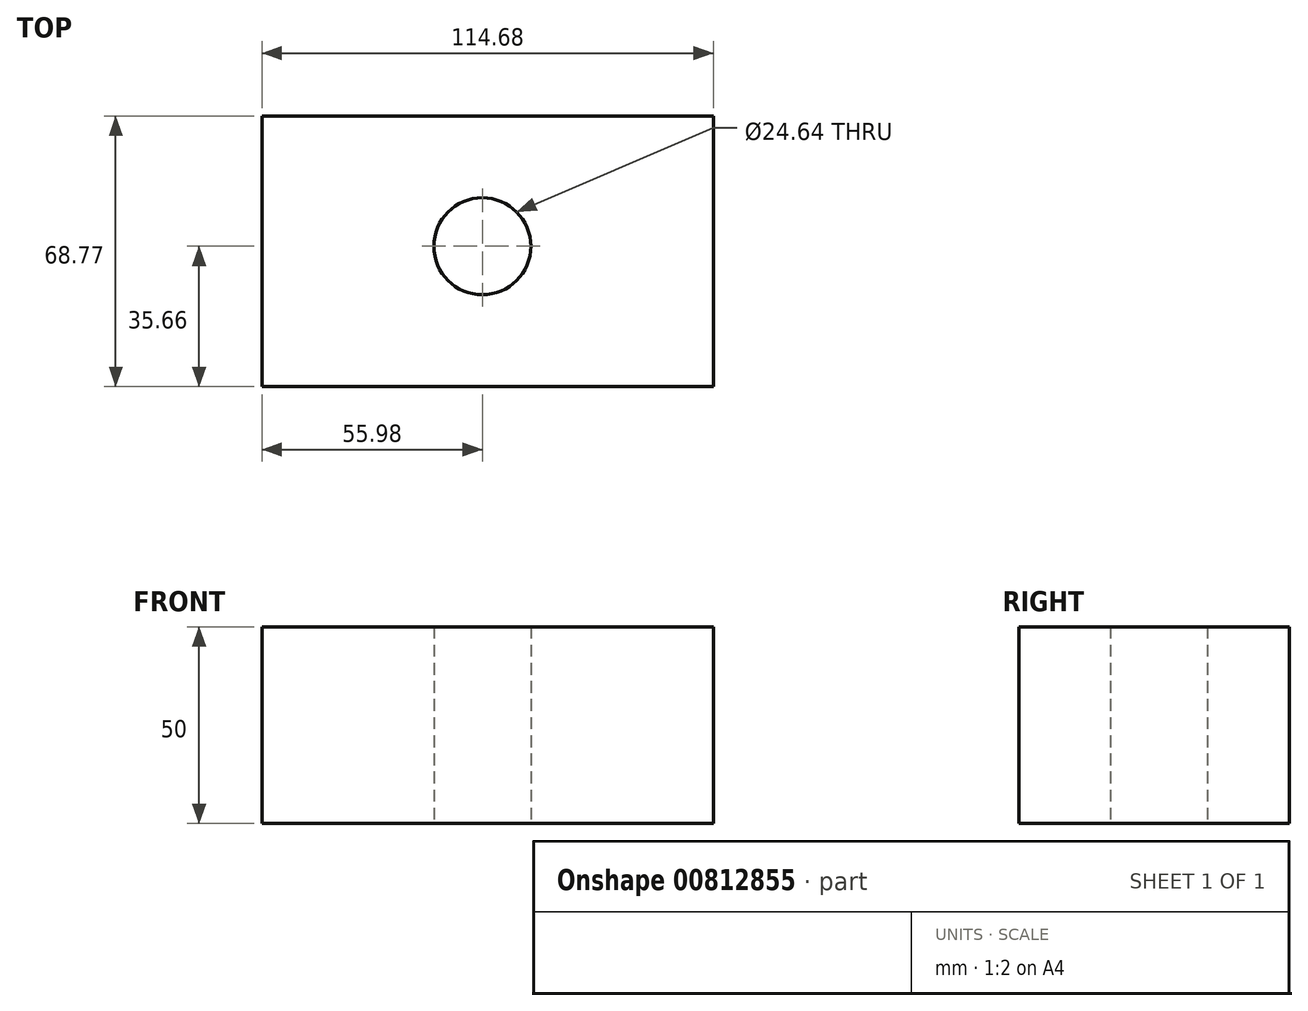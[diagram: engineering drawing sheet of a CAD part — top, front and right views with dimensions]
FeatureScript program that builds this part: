
annotation { "Feature Type Name" : "Feature", "Feature Type Description" : "" }
export const myFeature = defineFeature(function(context is Context, id is Id, definition is map)
    precondition{}
    {
        {
            var Q0;
            Q0=qCreatedBy(makeId("Top.planeOp"),FACE);
            var sketch = newSketch(context, id + "F0", { "sketchPlane" : qUnion([Q0])});
            skLineSegment(sketch, "E0.bottom", {"start": v(-55.98, 33.11) * mm, "end": v(58.7, 33.11) * mm});
            skLineSegment(sketch, "E0.top", {"start": v(-55.98, -35.66) * mm, "end": v(58.7, -35.66) * mm});
            skLineSegment(sketch, "E0.left", {"start": v(-55.98, 33.11) * mm, "end": v(-55.98, -35.66) * mm});
            skLineSegment(sketch, "E0.right", {"start": v(58.7, 33.11) * mm, "end": v(58.7, -35.66) * mm});
            skCircle(sketch, "E1", {"center": v(0, 0) * mm, "radius": 12.32 * mm});
            skSolve(sketch);
        }
        {
            var Q0;
            Q0=makeQuery(id+"F0.imprint","IMPRINT",FACE,{"disambiguationData":[TD([[makeQuery(id+"F0.imprint","IMPRINT",EDGE,{"derivedFrom":sQuery(id+"F0.wireOp",EDGE,"E0.bottom")}),-1.0]])]});
            extrude(context, id + "F1", {"entities" : qUnion([Q0]), "depth" : 50 * mm, "offsetDistance" : 25 * mm});
        }
    });
